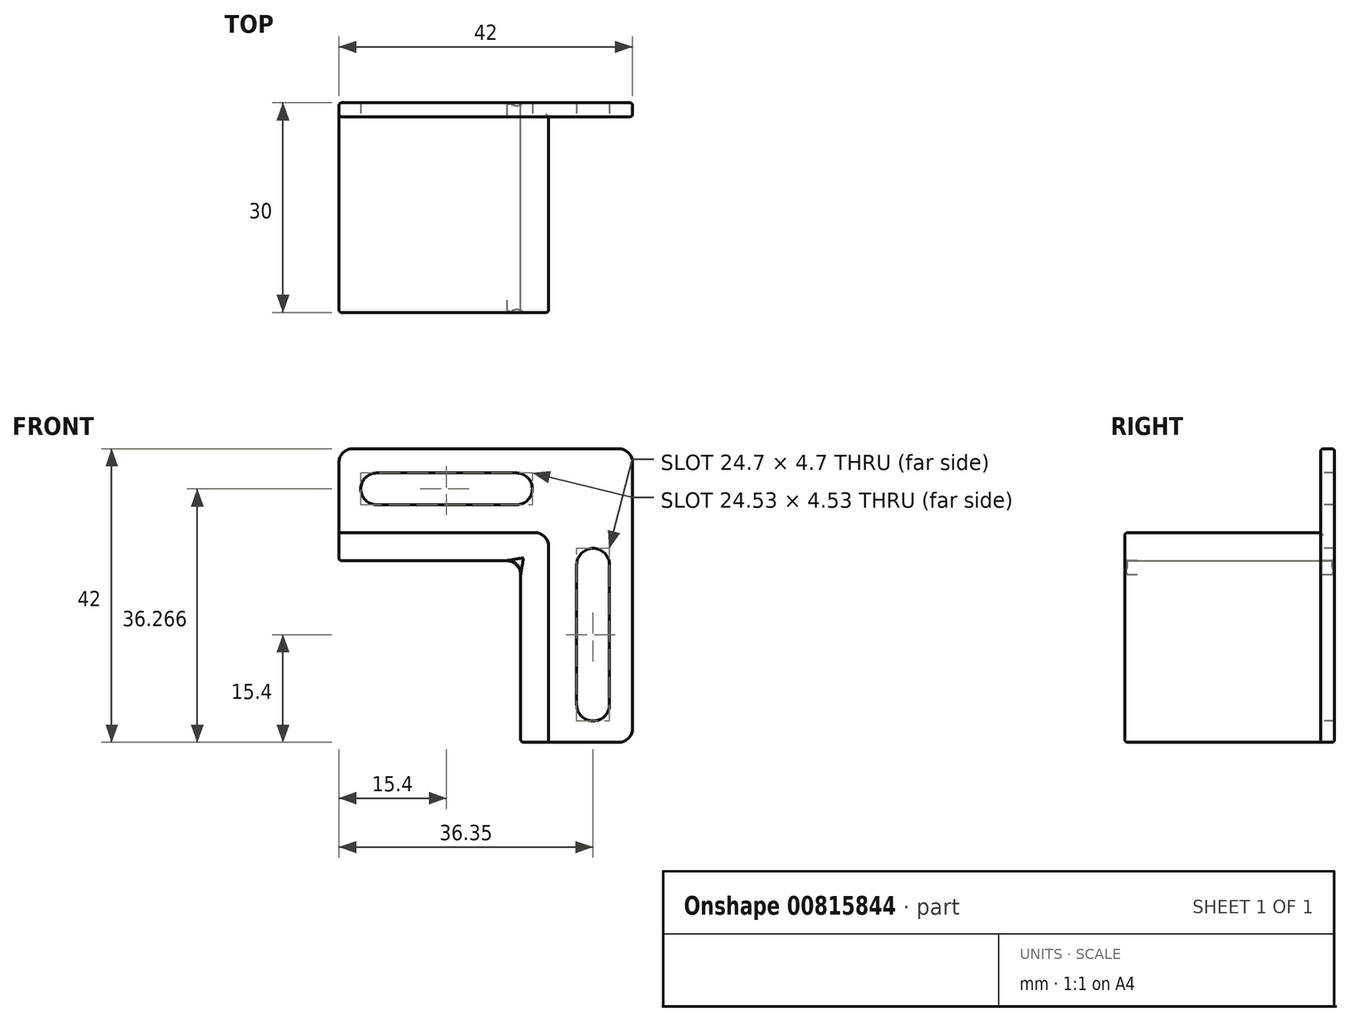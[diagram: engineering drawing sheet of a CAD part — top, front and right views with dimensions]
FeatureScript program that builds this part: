
annotation { "Feature Type Name" : "Feature", "Feature Type Description" : "" }
export const myFeature = defineFeature(function(context is Context, id is Id, definition is map)
    precondition{}
    {
        {
            var Q0;
            Q0=qCreatedBy(makeId("Front.planeOp"),FACE);
            var sketch = newSketch(context, id + "F0", { "sketchPlane" : qUnion([Q0])});
            skLineSegment(sketch, "E0.bottom", {"start": v(-15, 15) * mm, "end": v(15, 15) * mm});
            skLineSegment(sketch, "E0.right", {"start": v(15, 15) * mm, "end": v(15, -15) * mm});
            skPoint(sketch, "E0.middle", {"position": v(0, 0) * mm});
            skLineSegment(sketch, "E1.top", {"start": v(-15, 11) * mm, "end": v(11, 11) * mm});
            skLineSegment(sketch, "E1.right", {"start": v(11, -15) * mm, "end": v(11, 11) * mm});
            skLineSegment(sketch, "E2", {"start": v(-15, 15) * mm, "end": v(-15, 11) * mm});
            skLineSegment(sketch, "E3", {"start": v(11, -15) * mm, "end": v(15, -15) * mm});
            skLineSegment(sketch, "E4", {"start": v(-15, 15) * mm, "end": v(-15, 27) * mm});
            skLineSegment(sketch, "E5", {"start": v(-15, 27) * mm, "end": v(27, 27) * mm});
            skLineSegment(sketch, "E6", {"start": v(27, 27) * mm, "end": v(27, -15) * mm});
            skLineSegment(sketch, "E7", {"start": v(15, -15) * mm, "end": v(27, -15) * mm});
            skSolve(sketch);
        }
        {
            var Q0;
            Q0=makeQuery(id+"F0.imprint","IMPRINT",FACE,{"disambiguationData":[TD([[makeQuery(id+"F0.imprint","IMPRINT",EDGE,{"derivedFrom":sQuery(id+"F0.wireOp",EDGE,"E0.bottom")}),-1.0]])]});
            extrude(context, id + "F1", {"entities" : qUnion([Q0]), "depth" : 30 * mm, "offsetDistance" : 25 * mm});
        }
        {
            var Q0;
            Q0=makeQuery(id+"F0.imprint","IMPRINT",FACE,{"disambiguationData":[TD([[makeQuery(id+"F0.imprint","IMPRINT",EDGE,{"derivedFrom":sQuery(id+"F0.wireOp",EDGE,"E0.bottom")}),1.0]])]});
            extrude(context, id + "F2", {"entities" : qUnion([Q0]), "operationType" : NewBodyOperationType.ADD, "depth" : 2 * mm, "offsetDistance" : 25 * mm});
        }
        {
            var Q0;
            Q0=makeQuery(id+"F1.opExtrude","CAP_EDGE",EDGE,{"disambiguationData":[OSD([sQuery(id+"F0.wireOp",EDGE,"E0.bottom")])],"isStart":false});
            var Q1;
            Q1=makeQuery(id+"F1.opExtrude","CAP_EDGE",EDGE,{"disambiguationData":[OSD([sQuery(id+"F0.wireOp",EDGE,"E1.top")])],"isStart":false});
            var Q2;
            Q2=makeQuery(id+"F1.opExtrude","CAP_EDGE",EDGE,{"disambiguationData":[OSD([sQuery(id+"F0.wireOp",EDGE,"E1.right")])],"isStart":false});
            var Q3;
            Q3=makeQuery(id+"F1.opExtrude","CAP_EDGE",EDGE,{"disambiguationData":[OSD([sQuery(id+"F0.wireOp",EDGE,"E0.right")])],"isStart":false});
            var Q4;
            Q4=makeQuery(id+"F1.opExtrude","CAP_EDGE",EDGE,{"disambiguationData":[OSD([sQuery(id+"F0.wireOp",EDGE,"E3")])],"isStart":false});
            var Q5;
            Q5=makeQuery(id+"F1.opExtrude","CAP_EDGE",EDGE,{"disambiguationData":[OSD([sQuery(id+"F0.wireOp",EDGE,"E2")])],"isStart":false});
            var Q6;
            Q6=makeQuery(id+"F1.opExtrude","SWEPT_EDGE",EDGE,{"disambiguationData":[OSD([sQuery(id+"F0.wireOp",EDGE,"E0.right"),sQuery(id+"F0.wireOp",EDGE,"E3"),sQuery(id+"F0.wireOp",EDGE,"E7")])]});
            var Q7;
            Q7=makeQuery(id+"F1.opExtrude","SWEPT_EDGE",EDGE,{"disambiguationData":[OSD([sQuery(id+"F0.wireOp",EDGE,"E1.right"),sQuery(id+"F0.wireOp",EDGE,"E3")])]});
            var Q8;
            Q8=makeQuery(id+"F2.opExtrude","CAP_EDGE",EDGE,{"disambiguationData":[OSD([sQuery(id+"F0.wireOp",EDGE,"E7")])],"isStart":false});
            var Q9;
            Q9=makeQuery(id+"F2.boolean.opBoolean","MERGE",EDGE,{"derivedFrom":[makeQuery(id+"F1.opExtrude","CAP_EDGE",EDGE,{"disambiguationData":[OSD([sQuery(id+"F0.wireOp",EDGE,"E3")])],"isStart":true}),makeQuery(id+"F2.opExtrude","CAP_EDGE",EDGE,{"disambiguationData":[OSD([sQuery(id+"F0.wireOp",EDGE,"E7")])],"isStart":true})]});
            var Q10;
            Q10=makeQuery(id+"F1.opExtrude","CAP_EDGE",EDGE,{"disambiguationData":[OSD([sQuery(id+"F0.wireOp",EDGE,"E1.right")])],"isStart":true});
            var Q11;
            Q11=makeQuery(id+"F1.opExtrude","CAP_EDGE",EDGE,{"disambiguationData":[OSD([sQuery(id+"F0.wireOp",EDGE,"E1.top")])],"isStart":true});
            var Q12;
            Q12=makeQuery(id+"F1.opExtrude","SWEPT_EDGE",EDGE,{"disambiguationData":[OSD([sQuery(id+"F0.wireOp",EDGE,"E1.top"),sQuery(id+"F0.wireOp",EDGE,"E2")])]});
            var Q13;
            Q13=makeQuery(id+"F2.boolean.opBoolean","MERGE",EDGE,{"derivedFrom":[makeQuery(id+"F1.opExtrude","CAP_EDGE",EDGE,{"disambiguationData":[OSD([sQuery(id+"F0.wireOp",EDGE,"E2")])],"isStart":true}),makeQuery(id+"F2.opExtrude","CAP_EDGE",EDGE,{"disambiguationData":[OSD([sQuery(id+"F0.wireOp",EDGE,"E4")])],"isStart":true})]});
            var Q14;
            Q14=makeQuery(id+"F1.opExtrude","SWEPT_EDGE",EDGE,{"disambiguationData":[OSD([sQuery(id+"F0.wireOp",EDGE,"E0.bottom"),sQuery(id+"F0.wireOp",EDGE,"E2"),sQuery(id+"F0.wireOp",EDGE,"E4")])]});
            var Q15;
            Q15=makeQuery(id+"F2.opExtrude","CAP_EDGE",EDGE,{"disambiguationData":[OSD([sQuery(id+"F0.wireOp",EDGE,"E4")])],"isStart":false});
            var Q16;
            Q16=makeQuery(id+"F2.opExtrude","CAP_EDGE",EDGE,{"disambiguationData":[OSD([sQuery(id+"F0.wireOp",EDGE,"E5")])],"isStart":false});
            var Q17;
            Q17=makeQuery(id+"F2.opExtrude","CAP_EDGE",EDGE,{"disambiguationData":[OSD([sQuery(id+"F0.wireOp",EDGE,"E5")])],"isStart":true});
            var Q18;
            Q18=makeQuery(id+"F2.opExtrude","CAP_EDGE",EDGE,{"disambiguationData":[OSD([sQuery(id+"F0.wireOp",EDGE,"E6")])],"isStart":false});
            var Q19;
            Q19=makeQuery(id+"F2.opExtrude","CAP_EDGE",EDGE,{"disambiguationData":[OSD([sQuery(id+"F0.wireOp",EDGE,"E6")])],"isStart":true});
            fillet(context, id + "F3", {"entities" : qUnion([Q0, Q1, Q2, Q3, Q4, Q5, Q6, Q7, Q8, Q9, Q10, Q11, Q12, Q13, Q14, Q15, Q16, Q17, Q18, Q19]), "radius" : .4 * mm, "tangentPropagation" : true, "allowEdgeOverflow" : false});
        }
        {
            var Q0;
            Q0=makeQuery(id+"F1.opExtrude","SWEPT_EDGE",EDGE,{"disambiguationData":[OSD([sQuery(id+"F0.wireOp",EDGE,"E1.top"),sQuery(id+"F0.wireOp",EDGE,"E1.right")])]});
            var Q1;
            Q1=makeQuery(id+"F1.opExtrude","SWEPT_EDGE",EDGE,{"disambiguationData":[OSD([sQuery(id+"F0.wireOp",EDGE,"E0.bottom"),sQuery(id+"F0.wireOp",EDGE,"E0.right")])]});
            var Q2;
            Q2=makeQuery(id+"F2.opExtrude","SWEPT_EDGE",EDGE,{"disambiguationData":[OSD([sQuery(id+"F0.wireOp",EDGE,"E5"),sQuery(id+"F0.wireOp",EDGE,"E6")])]});
            var Q3;
            Q3=makeQuery(id+"F2.opExtrude","SWEPT_EDGE",EDGE,{"disambiguationData":[OSD([sQuery(id+"F0.wireOp",EDGE,"E6"),sQuery(id+"F0.wireOp",EDGE,"E7")])]});
            var Q4;
            Q4=makeQuery(id+"F2.opExtrude","SWEPT_EDGE",EDGE,{"disambiguationData":[OSD([sQuery(id+"F0.wireOp",EDGE,"E4"),sQuery(id+"F0.wireOp",EDGE,"E5")])]});
            fillet(context, id + "F4", {"entities" : qUnion([Q0, Q1, Q2, Q3, Q4]), "radius" : 2 * mm, "tangentPropagation" : true, "allowEdgeOverflow" : false});
        }
        {
            var Q0;
            Q0=makeQuery(id+"F2.opExtrude","CAP_FACE",FACE,{"disambiguationData":[OSD([sQuery(id+"F0.wireOp",EDGE,"E0.bottom"),sQuery(id+"F0.wireOp",EDGE,"E0.right"),sQuery(id+"F0.wireOp",EDGE,"E4"),sQuery(id+"F0.wireOp",EDGE,"E5"),sQuery(id+"F0.wireOp",EDGE,"E6"),sQuery(id+"F0.wireOp",EDGE,"E7")])],"isStart":false});
            var sketch = newSketch(context, id + "F5", { "sketchPlane" : qUnion([Q0])});
            skLineSegment(sketch, "E8.bottom", {"start": v(10.4, 23.53) * mm, "end": v(-9.6, 23.53) * mm});
            skLineSegment(sketch, "E8.top", {"start": v(10.4, 19) * mm, "end": v(-9.6, 19) * mm});
            skLineSegment(sketch, "E9.left", {"start": v(23.7, 10.4) * mm, "end": v(23.7, -9.6) * mm});
            skLineSegment(sketch, "E9.right", {"start": v(19, 10.4) * mm, "end": v(19, -9.6) * mm});
            skArc(sketch, "E10", {"start": v(10.4, 19) * mm, "mid": v(12.67, 21.27) * mm, "end": v(10.4, 23.53) * mm});
            skArc(sketch, "E11", {"start": v(-9.6, 23.53) * mm, "mid": v(-11.87, 21.27) * mm, "end": v(-9.6, 19) * mm});
            skArc(sketch, "E12", {"start": v(23.7, 10.4) * mm, "mid": v(21.35, 12.75) * mm, "end": v(19, 10.4) * mm});
            skArc(sketch, "E13", {"start": v(19, -9.6) * mm, "mid": v(21.35, -11.95) * mm, "end": v(23.7, -9.6) * mm});
            skSolve(sketch);
        }
        {
            var Q0;
            Q0=makeQuery(id+"F5.imprint","IMPRINT",FACE,{"disambiguationData":[TD([[makeQuery(id+"F5.imprint","IMPRINT",EDGE,{"derivedFrom":sQuery(id+"F5.wireOp",EDGE,"E8.bottom")}),1.0]])]});
            var Q1;
            Q1=makeQuery(id+"F5.imprint","IMPRINT",FACE,{"disambiguationData":[TD([[makeQuery(id+"F5.imprint","IMPRINT",EDGE,{"derivedFrom":sQuery(id+"F5.wireOp",EDGE,"E9.left")}),-1.0]])]});
            extrude(context, id + "F6", {"entities" : qUnion([Q0, Q1]), "operationType" : NewBodyOperationType.REMOVE, "oppositeDirection" : true, "depth" : 25 * mm, "offsetDistance" : 25 * mm});
        }
    });
